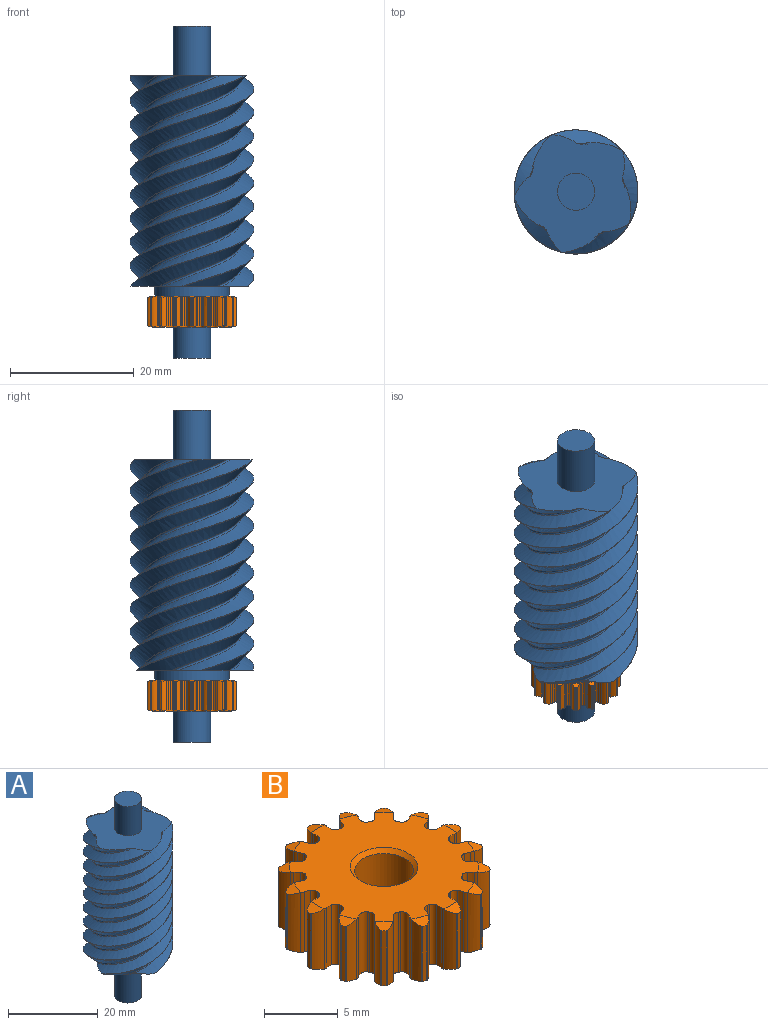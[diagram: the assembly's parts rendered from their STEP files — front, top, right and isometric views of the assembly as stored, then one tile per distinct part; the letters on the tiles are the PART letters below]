
ASSEMBLY  parts=2 mates=1
PART A: 33 faces, bbox 20.2x21.3x53.8 mm
  f0: cylinder r=10mm len=34mm, axis (0,0,-1), area -36.6mm2, adj f17,f22,f23,f26
  f1: bspline ~37.33x21.03mm, area 6.8mm2, adj f2,f17,f22,f26
  f2: bspline ~36.53x16.56mm, area 46.9mm2, adj f1,f3,f17,f22
  f3: bspline ~39.23x21.03mm, area 257mm2, adj f2,f4,f17,f22
  f4: cylinder r=10mm len=34mm, axis (0,0,-1), area -41.3mm2, adj f3,f17,f22,f27
  f5: bspline ~37.33x21.03mm, area 6.8mm2, adj f6,f17,f22,f27
  f6: bspline ~36.53x16.56mm, area 46.9mm2, adj f5,f7,f17,f22
  f7: bspline ~39.23x21.03mm, area 257mm2, adj f6,f8,f17,f22
  f8: cylinder r=10mm len=34mm, axis (0,0,-1), area -8.7mm2, adj f7,f17,f22,f28
  f9: bspline ~37.33x21.03mm, area 6.8mm2, adj f10,f17,f22,f28
  f10: bspline ~36.53x16.56mm, area 46.9mm2, adj f9,f11,f17,f22
  f11: bspline ~39.23x21.03mm, area 257mm2, adj f10,f12,f17,f22
  f12: cylinder r=10mm len=34mm, axis (0,0,-1), area -45.1mm2, adj f11,f17,f22,f29
  f13: bspline ~37.33x21.03mm, area 6.8mm2, adj f14,f17,f22,f29
  f14: bspline ~36.53x16.56mm, area 46.9mm2, adj f13,f15,f17,f22
  f15: bspline ~39.23x21.03mm, area 257mm2, adj f14,f16,f17,f22
  f16: cylinder r=10mm len=34mm, axis (0,0,-1), area -49.3mm2, adj f15,f17,f22,f30
  f17: plane 19.25x19.13mm, normal (0,0,1), area 217.7mm2, adj f0,f1,f2,f3,f4,f5,f6,f7
  f18: plane 6x6mm, normal (0,0,-1), area 28.3mm2, adj f19
  f19: cylinder r=3mm len=10mm, axis (0,0,-1), area 188.5mm2, adj f18,f20
  f20: plane 12x12mm, normal (0,0,-1), area 84.8mm2, adj f19,f21
  f21: cylinder r=6mm len=12mm, axis (0,0,-1), area 60.3mm2, adj f20,f22
  f22: plane 19.23x19.06mm, normal (0,0,-1), area 132.9mm2, adj f0,f1,f2,f3,f4,f5,f6,f7
  f23: bspline ~39.23x21.03mm, area 257mm2, adj f0,f17,f22,f24
  f24: bspline ~36.53x16.56mm, area 46.9mm2, adj f17,f22,f23,f25
  f25: bspline ~37.33x21.03mm, area 6.8mm2, adj f17,f22,f24,f30
  f26: bspline ~37.5x19.99mm, area 300.7mm2, adj f0,f1,f17,f22
  f27: bspline ~37.5x19.99mm, area 300.7mm2, adj f4,f5,f17,f22
  f28: bspline ~37.5x20mm, area 300.7mm2, adj f8,f9,f17,f22
  f29: bspline ~37.5x19.97mm, area 300.7mm2, adj f12,f13,f17,f22
  f30: bspline ~37.5x20mm, area 300.7mm2, adj f16,f17,f22,f25
  f31: cylinder r=3mm len=8mm, axis (0,0,-1), area 150.8mm2, adj f17,f32
  f32: plane 6x6mm, normal (0,0,1), area 28.3mm2, adj f31
PART B: 229 faces, bbox 14.4x14.4x5 mm
  f0: plane 12.8x12.8mm, normal (0,0,-1), area 96.1mm2, adj f1,f2,f3,f4,f5,f6,f7,f8
  f1: cone r=9.2mm half-angle=75deg, axis (0,0,1), area 0.7mm2, adj f0,f17,f63,f64,f65,f208
  f2: cone r=9.2mm half-angle=75deg, axis (0,0,1), area 0.7mm2, adj f0,f60,f61,f62,f199,f200
  f3: cone r=9.2mm half-angle=75deg, axis (0,0,1), area 0.7mm2, adj f0,f57,f58,f59,f190,f191
  f4: cone r=9.2mm half-angle=75deg, axis (0,0,1), area 0.7mm2, adj f0,f54,f55,f56,f181,f182
  f5: cone r=9.2mm half-angle=75deg, axis (0,0,1), area 0.7mm2, adj f0,f51,f52,f53,f172,f173
  f6: cone r=9.2mm half-angle=75deg, axis (0,0,1), area 0.7mm2, adj f0,f48,f49,f50,f163,f164
  f7: cone r=9.2mm half-angle=75deg, axis (0,0,1), area 0.7mm2, adj f0,f45,f46,f47,f154,f155
  f8: cone r=9.2mm half-angle=75deg, axis (0,0,1), area 0.7mm2, adj f0,f42,f43,f44,f145,f146
  f9: cone r=9.2mm half-angle=75deg, axis (0,0,1), area 0.7mm2, adj f0,f39,f40,f41,f136,f137
  f10: cone r=9.2mm half-angle=75deg, axis (0,0,1), area 0.7mm2, adj f0,f36,f37,f38,f127,f128
  f11: cone r=9.2mm half-angle=75deg, axis (0,0,1), area 0.7mm2, adj f0,f33,f34,f35,f118,f119
  f12: cone r=9.2mm half-angle=75deg, axis (0,0,1), area 0.7mm2, adj f0,f30,f31,f32,f109,f110
  f13: cone r=9.2mm half-angle=75deg, axis (0,0,1), area 0.7mm2, adj f0,f27,f28,f29,f100,f101
  f14: cone r=9.2mm half-angle=75deg, axis (0,0,1), area 0.7mm2, adj f0,f24,f25,f26,f91,f92
  f15: cone r=9.2mm half-angle=75deg, axis (0,0,1), area 0.7mm2, adj f0,f21,f22,f23,f82,f83
  f16: cone r=9.2mm half-angle=75deg, axis (0,0,1), area 0.7mm2, adj f0,f18,f19,f20,f73,f74
  f17: cylinder r=0.08mm len=4.59mm, axis (0,0,-1), area 0.3mm2, adj f1,f64,f65,f225
  f18: cylinder r=0.08mm len=4.59mm, axis (0,0,-1), area 0.3mm2, adj f16,f19,f73,f210
  f19: cylinder r=7.2mm len=4.57mm, axis (0,0,-1), area 1.4mm2, adj f16,f18,f20,f210
  f20: cylinder r=0.08mm len=4.59mm, axis (0,0,-1), area 0.3mm2, adj f16,f19,f74,f210
  f21: cylinder r=0.08mm len=4.59mm, axis (0,0,-1), area 0.3mm2, adj f15,f22,f82,f211
  f22: cylinder r=7.2mm len=4.57mm, axis (0,0,-1), area 1.4mm2, adj f15,f21,f23,f211
  f23: cylinder r=0.08mm len=4.59mm, axis (0,0,-1), area 0.3mm2, adj f15,f22,f83,f211
  f24: cylinder r=0.08mm len=4.59mm, axis (0,0,-1), area 0.3mm2, adj f14,f25,f91,f212
  f25: cylinder r=7.2mm len=4.57mm, axis (0,0,-1), area 1.4mm2, adj f14,f24,f26,f212
  f26: cylinder r=0.08mm len=4.59mm, axis (0,0,-1), area 0.3mm2, adj f14,f25,f92,f212
  f27: cylinder r=0.08mm len=4.59mm, axis (0,0,-1), area 0.3mm2, adj f13,f28,f100,f213
  f28: cylinder r=7.2mm len=4.57mm, axis (0,0,-1), area 1.4mm2, adj f13,f27,f29,f213
  f29: cylinder r=0.08mm len=4.59mm, axis (0,0,-1), area 0.3mm2, adj f13,f28,f101,f213
  f30: cylinder r=0.08mm len=4.59mm, axis (0,0,-1), area 0.3mm2, adj f12,f31,f109,f214
  f31: cylinder r=7.2mm len=4.57mm, axis (0,0,-1), area 1.4mm2, adj f12,f30,f32,f214
  f32: cylinder r=0.08mm len=4.59mm, axis (0,0,-1), area 0.3mm2, adj f12,f31,f110,f214
  f33: cylinder r=0.08mm len=4.59mm, axis (0,0,-1), area 0.3mm2, adj f11,f34,f118,f215
  f34: cylinder r=7.2mm len=4.57mm, axis (0,0,-1), area 1.4mm2, adj f11,f33,f35,f215
  f35: cylinder r=0.08mm len=4.59mm, axis (0,0,-1), area 0.3mm2, adj f11,f34,f119,f215
  f36: cylinder r=0.08mm len=4.59mm, axis (0,0,-1), area 0.3mm2, adj f10,f37,f127,f216
  f37: cylinder r=7.2mm len=4.57mm, axis (0,0,-1), area 1.4mm2, adj f10,f36,f38,f216
  f38: cylinder r=0.08mm len=4.59mm, axis (0,0,-1), area 0.3mm2, adj f10,f37,f128,f216
  f39: cylinder r=0.08mm len=4.59mm, axis (0,0,-1), area 0.3mm2, adj f9,f40,f136,f217
  f40: cylinder r=7.2mm len=4.57mm, axis (0,0,-1), area 1.4mm2, adj f9,f39,f41,f217
  f41: cylinder r=0.08mm len=4.59mm, axis (0,0,-1), area 0.3mm2, adj f9,f40,f137,f217
  f42: cylinder r=0.08mm len=4.59mm, axis (0,0,-1), area 0.3mm2, adj f8,f43,f145,f218
  f43: cylinder r=7.2mm len=4.57mm, axis (0,0,-1), area 1.4mm2, adj f8,f42,f44,f218
  f44: cylinder r=0.08mm len=4.59mm, axis (0,0,-1), area 0.3mm2, adj f8,f43,f146,f218
  f45: cylinder r=0.08mm len=4.59mm, axis (0,0,-1), area 0.3mm2, adj f7,f46,f154,f219
  f46: cylinder r=7.2mm len=4.57mm, axis (0,0,-1), area 1.4mm2, adj f7,f45,f47,f219
  f47: cylinder r=0.08mm len=4.59mm, axis (0,0,-1), area 0.3mm2, adj f7,f46,f155,f219
  f48: cylinder r=0.08mm len=4.59mm, axis (0,0,-1), area 0.3mm2, adj f6,f49,f163,f220
  f49: cylinder r=7.2mm len=4.57mm, axis (0,0,-1), area 1.4mm2, adj f6,f48,f50,f220
  f50: cylinder r=0.08mm len=4.59mm, axis (0,0,-1), area 0.3mm2, adj f6,f49,f164,f220
  f51: cylinder r=0.08mm len=4.59mm, axis (0,0,-1), area 0.3mm2, adj f5,f52,f172,f221
  f52: cylinder r=7.2mm len=4.57mm, axis (0,0,-1), area 1.4mm2, adj f5,f51,f53,f221
  f53: cylinder r=0.08mm len=4.59mm, axis (0,0,-1), area 0.3mm2, adj f5,f52,f173,f221
  f54: cylinder r=0.08mm len=4.59mm, axis (0,0,-1), area 0.3mm2, adj f4,f55,f181,f222
  f55: cylinder r=7.2mm len=4.57mm, axis (0,0,-1), area 1.4mm2, adj f4,f54,f56,f222
  f56: cylinder r=0.08mm len=4.59mm, axis (0,0,-1), area 0.3mm2, adj f4,f55,f182,f222
  f57: cylinder r=0.08mm len=4.59mm, axis (0,0,-1), area 0.3mm2, adj f3,f58,f190,f223
  f58: cylinder r=7.2mm len=4.57mm, axis (0,0,-1), area 1.4mm2, adj f3,f57,f59,f223
  f59: cylinder r=0.08mm len=4.59mm, axis (0,0,-1), area 0.3mm2, adj f3,f58,f191,f223
  f60: cylinder r=0.08mm len=4.59mm, axis (0,0,-1), area 0.3mm2, adj f2,f61,f199,f224
  f61: cylinder r=7.2mm len=4.57mm, axis (0,0,-1), area 1.4mm2, adj f2,f60,f62,f224
  f62: cylinder r=0.08mm len=4.59mm, axis (0,0,-1), area 0.3mm2, adj f2,f61,f200,f224
  f63: cylinder r=0.08mm len=4.59mm, axis (0,0,-1), area 0.3mm2, adj f1,f64,f208,f225
  f64: cylinder r=7.2mm len=4.57mm, axis (0,0,-1), area 1.4mm2, adj f1,f17,f63,f225
  f65: cylinder r=2mm len=5mm, axis (0,0,-1), area 4.4mm2, adj f1,f17,f66,f225
  f66: cylinder r=0.65mm len=5mm, axis (0,0,-1), area 1.3mm2, adj f0,f65,f67,f209
  f67: cylinder r=1.6mm len=5mm, axis (0,0,-1), area 2.4mm2, adj f0,f66,f68,f209
  f68: cylinder r=0.4mm len=5mm, axis (0,0,-1), area 2.5mm2, adj f0,f67,f69,f209
  f69: cylinder r=5.4mm len=5mm, axis (0,0,-1), area 0.9mm2, adj f0,f68,f70,f209
  f70: cylinder r=0.4mm len=5mm, axis (0,0,-1), area 2.5mm2, adj f0,f69,f71,f209
  f71: cylinder r=1.6mm len=5mm, axis (0,0,-1), area 2.4mm2, adj f0,f70,f72,f209
  f72: cylinder r=0.65mm len=5mm, axis (0,0,-1), area 1.3mm2, adj f0,f71,f73,f209
  f73: cylinder r=2mm len=5mm, axis (0,0,-1), area 4.4mm2, adj f16,f18,f72,f210
  f74: cylinder r=2mm len=5mm, axis (0,0,-1), area 4.4mm2, adj f16,f20,f75,f210
  f75: cylinder r=0.65mm len=5mm, axis (0,0,-1), area 1.3mm2, adj f0,f74,f76,f209
  f76: cylinder r=1.6mm len=5mm, axis (0,0,-1), area 2.4mm2, adj f0,f75,f77,f209
  f77: cylinder r=0.4mm len=5mm, axis (0,0,-1), area 2.5mm2, adj f0,f76,f78,f209
  f78: cylinder r=5.4mm len=5mm, axis (0,0,-1), area 0.9mm2, adj f0,f77,f79,f209
  f79: cylinder r=0.4mm len=5mm, axis (0,0,-1), area 2.5mm2, adj f0,f78,f80,f209
  f80: cylinder r=1.6mm len=5mm, axis (0,0,-1), area 2.4mm2, adj f0,f79,f81,f209
  f81: cylinder r=0.65mm len=5mm, axis (0,0,-1), area 1.3mm2, adj f0,f80,f82,f209
  f82: cylinder r=2mm len=5mm, axis (0,0,-1), area 4.4mm2, adj f15,f21,f81,f211
  f83: cylinder r=2mm len=5mm, axis (0,0,-1), area 4.4mm2, adj f15,f23,f84,f211
  f84: cylinder r=0.65mm len=5mm, axis (0,0,-1), area 1.3mm2, adj f0,f83,f85,f209
  f85: cylinder r=1.6mm len=5mm, axis (0,0,-1), area 2.4mm2, adj f0,f84,f86,f209
  f86: cylinder r=0.4mm len=5mm, axis (0,0,-1), area 2.5mm2, adj f0,f85,f87,f209
  f87: cylinder r=5.4mm len=5mm, axis (0,0,-1), area 0.9mm2, adj f0,f86,f88,f209
  f88: cylinder r=0.4mm len=5mm, axis (0,0,-1), area 2.5mm2, adj f0,f87,f89,f209
  f89: cylinder r=1.6mm len=5mm, axis (0,0,-1), area 2.4mm2, adj f0,f88,f90,f209
  f90: cylinder r=0.65mm len=5mm, axis (0,0,-1), area 1.3mm2, adj f0,f89,f91,f209
  f91: cylinder r=2mm len=5mm, axis (0,0,-1), area 4.4mm2, adj f14,f24,f90,f212
  f92: cylinder r=2mm len=5mm, axis (0,0,-1), area 4.4mm2, adj f14,f26,f93,f212
  f93: cylinder r=0.65mm len=5mm, axis (0,0,-1), area 1.3mm2, adj f0,f92,f94,f209
  f94: cylinder r=1.6mm len=5mm, axis (0,0,-1), area 2.4mm2, adj f0,f93,f95,f209
  f95: cylinder r=0.4mm len=5mm, axis (0,0,-1), area 2.5mm2, adj f0,f94,f96,f209
  f96: cylinder r=5.4mm len=5mm, axis (0,0,-1), area 0.9mm2, adj f0,f95,f97,f209
  f97: cylinder r=0.4mm len=5mm, axis (0,0,-1), area 2.5mm2, adj f0,f96,f98,f209
  f98: cylinder r=1.6mm len=5mm, axis (0,0,-1), area 2.4mm2, adj f0,f97,f99,f209
  f99: cylinder r=0.65mm len=5mm, axis (0,0,-1), area 1.3mm2, adj f0,f98,f100,f209
  f100: cylinder r=2mm len=5mm, axis (0,0,-1), area 4.4mm2, adj f13,f27,f99,f213
  f101: cylinder r=2mm len=5mm, axis (0,0,-1), area 4.4mm2, adj f13,f29,f102,f213
  f102: cylinder r=0.65mm len=5mm, axis (0,0,-1), area 1.3mm2, adj f0,f101,f103,f209
  f103: cylinder r=1.6mm len=5mm, axis (0,0,-1), area 2.4mm2, adj f0,f102,f104,f209
  f104: cylinder r=0.4mm len=5mm, axis (0,0,-1), area 2.5mm2, adj f0,f103,f105,f209
  f105: cylinder r=5.4mm len=5mm, axis (0,0,-1), area 0.9mm2, adj f0,f104,f106,f209
  f106: cylinder r=0.4mm len=5mm, axis (0,0,-1), area 2.5mm2, adj f0,f105,f107,f209
  f107: cylinder r=1.6mm len=5mm, axis (0,0,-1), area 2.4mm2, adj f0,f106,f108,f209
  f108: cylinder r=0.65mm len=5mm, axis (0,0,-1), area 1.3mm2, adj f0,f107,f109,f209
  f109: cylinder r=2mm len=5mm, axis (0,0,-1), area 4.4mm2, adj f12,f30,f108,f214
  f110: cylinder r=2mm len=5mm, axis (0,0,-1), area 4.4mm2, adj f12,f32,f111,f214
  f111: cylinder r=0.65mm len=5mm, axis (0,0,-1), area 1.3mm2, adj f0,f110,f112,f209
  f112: cylinder r=1.6mm len=5mm, axis (0,0,-1), area 2.4mm2, adj f0,f111,f113,f209
  f113: cylinder r=0.4mm len=5mm, axis (0,0,-1), area 2.5mm2, adj f0,f112,f114,f209
  f114: cylinder r=5.4mm len=5mm, axis (0,0,-1), area 0.9mm2, adj f0,f113,f115,f209
  f115: cylinder r=0.4mm len=5mm, axis (0,0,-1), area 2.5mm2, adj f0,f114,f116,f209
  f116: cylinder r=1.6mm len=5mm, axis (0,0,-1), area 2.4mm2, adj f0,f115,f117,f209
  f117: cylinder r=0.65mm len=5mm, axis (0,0,-1), area 1.3mm2, adj f0,f116,f118,f209
  f118: cylinder r=2mm len=5mm, axis (0,0,-1), area 4.4mm2, adj f11,f33,f117,f215
  f119: cylinder r=2mm len=5mm, axis (0,0,-1), area 4.4mm2, adj f11,f35,f120,f215
  f120: cylinder r=0.65mm len=5mm, axis (0,0,-1), area 1.3mm2, adj f0,f119,f121,f209
  f121: cylinder r=1.6mm len=5mm, axis (0,0,-1), area 2.4mm2, adj f0,f120,f122,f209
  f122: cylinder r=0.4mm len=5mm, axis (0,0,-1), area 2.5mm2, adj f0,f121,f123,f209
  f123: cylinder r=5.4mm len=5mm, axis (0,0,-1), area 0.9mm2, adj f0,f122,f124,f209
  f124: cylinder r=0.4mm len=5mm, axis (0,0,-1), area 2.5mm2, adj f0,f123,f125,f209
  f125: cylinder r=1.6mm len=5mm, axis (0,0,-1), area 2.4mm2, adj f0,f124,f126,f209
  f126: cylinder r=0.65mm len=5mm, axis (0,0,-1), area 1.3mm2, adj f0,f125,f127,f209
  f127: cylinder r=2mm len=5mm, axis (0,0,-1), area 4.4mm2, adj f10,f36,f126,f216
  f128: cylinder r=2mm len=5mm, axis (0,0,-1), area 4.4mm2, adj f10,f38,f129,f216
  f129: cylinder r=0.65mm len=5mm, axis (0,0,-1), area 1.3mm2, adj f0,f128,f130,f209
  f130: cylinder r=1.6mm len=5mm, axis (0,0,-1), area 2.4mm2, adj f0,f129,f131,f209
  f131: cylinder r=0.4mm len=5mm, axis (0,0,-1), area 2.5mm2, adj f0,f130,f132,f209
  f132: cylinder r=5.4mm len=5mm, axis (0,0,-1), area 0.9mm2, adj f0,f131,f133,f209
  f133: cylinder r=0.4mm len=5mm, axis (0,0,-1), area 2.5mm2, adj f0,f132,f134,f209
  f134: cylinder r=1.6mm len=5mm, axis (0,0,-1), area 2.4mm2, adj f0,f133,f135,f209
  f135: cylinder r=0.65mm len=5mm, axis (0,0,-1), area 1.3mm2, adj f0,f134,f136,f209
  f136: cylinder r=2mm len=5mm, axis (0,0,-1), area 4.4mm2, adj f9,f39,f135,f217
  f137: cylinder r=2mm len=5mm, axis (0,0,-1), area 4.4mm2, adj f9,f41,f138,f217
  f138: cylinder r=0.65mm len=5mm, axis (0,0,-1), area 1.3mm2, adj f0,f137,f139,f209
  f139: cylinder r=1.6mm len=5mm, axis (0,0,-1), area 2.4mm2, adj f0,f138,f140,f209
  f140: cylinder r=0.4mm len=5mm, axis (0,0,-1), area 2.5mm2, adj f0,f139,f141,f209
  f141: cylinder r=5.4mm len=5mm, axis (0,0,-1), area 0.9mm2, adj f0,f140,f142,f209
  f142: cylinder r=0.4mm len=5mm, axis (0,0,-1), area 2.5mm2, adj f0,f141,f143,f209
  f143: cylinder r=1.6mm len=5mm, axis (0,0,-1), area 2.4mm2, adj f0,f142,f144,f209
  f144: cylinder r=0.65mm len=5mm, axis (0,0,-1), area 1.3mm2, adj f0,f143,f145,f209
  f145: cylinder r=2mm len=5mm, axis (0,0,-1), area 4.4mm2, adj f8,f42,f144,f218
  f146: cylinder r=2mm len=5mm, axis (0,0,-1), area 4.4mm2, adj f8,f44,f147,f218
  f147: cylinder r=0.65mm len=5mm, axis (0,0,-1), area 1.3mm2, adj f0,f146,f148,f209
  f148: cylinder r=1.6mm len=5mm, axis (0,0,-1), area 2.4mm2, adj f0,f147,f149,f209
  f149: cylinder r=0.4mm len=5mm, axis (0,0,-1), area 2.5mm2, adj f0,f148,f150,f209
  f150: cylinder r=5.4mm len=5mm, axis (0,0,-1), area 0.9mm2, adj f0,f149,f151,f209
  f151: cylinder r=0.4mm len=5mm, axis (0,0,-1), area 2.5mm2, adj f0,f150,f152,f209
  f152: cylinder r=1.6mm len=5mm, axis (0,0,-1), area 2.4mm2, adj f0,f151,f153,f209
  f153: cylinder r=0.65mm len=5mm, axis (0,0,-1), area 1.3mm2, adj f0,f152,f154,f209
  f154: cylinder r=2mm len=5mm, axis (0,0,-1), area 4.4mm2, adj f7,f45,f153,f219
  f155: cylinder r=2mm len=5mm, axis (0,0,-1), area 4.4mm2, adj f7,f47,f156,f219
  f156: cylinder r=0.65mm len=5mm, axis (0,0,-1), area 1.3mm2, adj f0,f155,f157,f209
  f157: cylinder r=1.6mm len=5mm, axis (0,0,-1), area 2.4mm2, adj f0,f156,f158,f209
  f158: cylinder r=0.4mm len=5mm, axis (0,0,-1), area 2.5mm2, adj f0,f157,f159,f209
  f159: cylinder r=5.4mm len=5mm, axis (0,0,-1), area 0.9mm2, adj f0,f158,f160,f209
  f160: cylinder r=0.4mm len=5mm, axis (0,0,-1), area 2.5mm2, adj f0,f159,f161,f209
  f161: cylinder r=1.6mm len=5mm, axis (0,0,-1), area 2.4mm2, adj f0,f160,f162,f209
  f162: cylinder r=0.65mm len=5mm, axis (0,0,-1), area 1.3mm2, adj f0,f161,f163,f209
  f163: cylinder r=2mm len=5mm, axis (0,0,-1), area 4.4mm2, adj f6,f48,f162,f220
  f164: cylinder r=2mm len=5mm, axis (0,0,-1), area 4.4mm2, adj f6,f50,f165,f220
  f165: cylinder r=0.65mm len=5mm, axis (0,0,-1), area 1.3mm2, adj f0,f164,f166,f209
  f166: cylinder r=1.6mm len=5mm, axis (0,0,-1), area 2.4mm2, adj f0,f165,f167,f209
  f167: cylinder r=0.4mm len=5mm, axis (0,0,-1), area 2.5mm2, adj f0,f166,f168,f209
  f168: cylinder r=5.4mm len=5mm, axis (0,0,-1), area 0.9mm2, adj f0,f167,f169,f209
  f169: cylinder r=0.4mm len=5mm, axis (0,0,-1), area 2.5mm2, adj f0,f168,f170,f209
  f170: cylinder r=1.6mm len=5mm, axis (0,0,-1), area 2.4mm2, adj f0,f169,f171,f209
  f171: cylinder r=0.65mm len=5mm, axis (0,0,-1), area 1.3mm2, adj f0,f170,f172,f209
  f172: cylinder r=2mm len=5mm, axis (0,0,-1), area 4.4mm2, adj f5,f51,f171,f221
  f173: cylinder r=2mm len=5mm, axis (0,0,-1), area 4.4mm2, adj f5,f53,f174,f221
  f174: cylinder r=0.65mm len=5mm, axis (0,0,-1), area 1.3mm2, adj f0,f173,f175,f209
  f175: cylinder r=1.6mm len=5mm, axis (0,0,-1), area 2.4mm2, adj f0,f174,f176,f209
  f176: cylinder r=0.4mm len=5mm, axis (0,0,-1), area 2.5mm2, adj f0,f175,f177,f209
  f177: cylinder r=5.4mm len=5mm, axis (0,0,-1), area 0.9mm2, adj f0,f176,f178,f209
  f178: cylinder r=0.4mm len=5mm, axis (0,0,-1), area 2.5mm2, adj f0,f177,f179,f209
  f179: cylinder r=1.6mm len=5mm, axis (0,0,-1), area 2.4mm2, adj f0,f178,f180,f209
  f180: cylinder r=0.65mm len=5mm, axis (0,0,-1), area 1.3mm2, adj f0,f179,f181,f209
  f181: cylinder r=2mm len=5mm, axis (0,0,-1), area 4.4mm2, adj f4,f54,f180,f222
  f182: cylinder r=2mm len=5mm, axis (0,0,-1), area 4.4mm2, adj f4,f56,f183,f222
  f183: cylinder r=0.65mm len=5mm, axis (0,0,-1), area 1.3mm2, adj f0,f182,f184,f209
  f184: cylinder r=1.6mm len=5mm, axis (0,0,-1), area 2.4mm2, adj f0,f183,f185,f209
  f185: cylinder r=0.4mm len=5mm, axis (0,0,-1), area 2.5mm2, adj f0,f184,f186,f209
  f186: cylinder r=5.4mm len=5mm, axis (0,0,-1), area 0.9mm2, adj f0,f185,f187,f209
  f187: cylinder r=0.4mm len=5mm, axis (0,0,-1), area 2.5mm2, adj f0,f186,f188,f209
  f188: cylinder r=1.6mm len=5mm, axis (0,0,-1), area 2.4mm2, adj f0,f187,f189,f209
  f189: cylinder r=0.65mm len=5mm, axis (0,0,-1), area 1.3mm2, adj f0,f188,f190,f209
  f190: cylinder r=2mm len=5mm, axis (0,0,-1), area 4.4mm2, adj f3,f57,f189,f223
  f191: cylinder r=2mm len=5mm, axis (0,0,-1), area 4.4mm2, adj f3,f59,f192,f223
  f192: cylinder r=0.65mm len=5mm, axis (0,0,-1), area 1.3mm2, adj f0,f191,f193,f209
  f193: cylinder r=1.6mm len=5mm, axis (0,0,-1), area 2.4mm2, adj f0,f192,f194,f209
  f194: cylinder r=0.4mm len=5mm, axis (0,0,-1), area 2.5mm2, adj f0,f193,f195,f209
  f195: cylinder r=5.4mm len=5mm, axis (0,0,-1), area 0.9mm2, adj f0,f194,f196,f209
  f196: cylinder r=0.4mm len=5mm, axis (0,0,-1), area 2.5mm2, adj f0,f195,f197,f209
  f197: cylinder r=1.6mm len=5mm, axis (0,0,-1), area 2.4mm2, adj f0,f196,f198,f209
  f198: cylinder r=0.65mm len=5mm, axis (0,0,-1), area 1.3mm2, adj f0,f197,f199,f209
  f199: cylinder r=2mm len=5mm, axis (0,0,-1), area 4.4mm2, adj f2,f60,f198,f224
  f200: cylinder r=2mm len=5mm, axis (0,0,-1), area 4.4mm2, adj f2,f62,f201,f224
  f201: cylinder r=0.65mm len=5mm, axis (0,0,-1), area 1.3mm2, adj f0,f200,f202,f209
  f202: cylinder r=1.6mm len=5mm, axis (0,0,-1), area 2.4mm2, adj f0,f201,f203,f209
  f203: cylinder r=0.4mm len=5mm, axis (0,0,-1), area 2.5mm2, adj f0,f202,f204,f209
  f204: cylinder r=5.4mm len=5mm, axis (0,0,-1), area 0.9mm2, adj f0,f203,f205,f209
  f205: cylinder r=0.4mm len=5mm, axis (0,0,-1), area 2.5mm2, adj f0,f204,f206,f209
  f206: cylinder r=1.6mm len=5mm, axis (0,0,-1), area 2.4mm2, adj f0,f205,f207,f209
  f207: cylinder r=0.65mm len=5mm, axis (0,0,-1), area 1.3mm2, adj f0,f206,f208,f209
  f208: cylinder r=2mm len=5mm, axis (0,0,-1), area 4.4mm2, adj f1,f63,f207,f225
  f209: plane 12.8x12.8mm, normal (0,0,1), area 96.1mm2, adj f66,f67,f68,f69,f70,f71,f72,f75
  f210: cone r=6.4mm half-angle=75deg, axis (0,0,-1), area 0.7mm2, adj f18,f19,f20,f73,f74,f209
  f211: cone r=6.4mm half-angle=75deg, axis (0,0,-1), area 0.7mm2, adj f21,f22,f23,f82,f83,f209
  f212: cone r=6.4mm half-angle=75deg, axis (0,0,-1), area 0.7mm2, adj f24,f25,f26,f91,f92,f209
  f213: cone r=6.4mm half-angle=75deg, axis (0,0,-1), area 0.7mm2, adj f27,f28,f29,f100,f101,f209
  f214: cone r=6.4mm half-angle=75deg, axis (0,0,-1), area 0.7mm2, adj f30,f31,f32,f109,f110,f209
  f215: cone r=6.4mm half-angle=75deg, axis (0,0,-1), area 0.7mm2, adj f33,f34,f35,f118,f119,f209
  f216: cone r=6.4mm half-angle=75deg, axis (0,0,-1), area 0.7mm2, adj f36,f37,f38,f127,f128,f209
  f217: cone r=6.4mm half-angle=75deg, axis (0,0,-1), area 0.7mm2, adj f39,f40,f41,f136,f137,f209
  f218: cone r=6.4mm half-angle=75deg, axis (0,0,-1), area 0.7mm2, adj f42,f43,f44,f145,f146,f209
  f219: cone r=6.4mm half-angle=75deg, axis (0,0,-1), area 0.7mm2, adj f45,f46,f47,f154,f155,f209
  f220: cone r=6.4mm half-angle=75deg, axis (0,0,-1), area 0.7mm2, adj f48,f49,f50,f163,f164,f209
  f221: cone r=6.4mm half-angle=75deg, axis (0,0,-1), area 0.7mm2, adj f51,f52,f53,f172,f173,f209
  f222: cone r=6.4mm half-angle=75deg, axis (0,0,-1), area 0.7mm2, adj f54,f55,f56,f181,f182,f209
  f223: cone r=6.4mm half-angle=75deg, axis (0,0,-1), area 0.7mm2, adj f57,f58,f59,f190,f191,f209
  f224: cone r=6.4mm half-angle=75deg, axis (0,0,-1), area 0.7mm2, adj f60,f61,f62,f199,f200,f209
  f225: cone r=6.4mm half-angle=75deg, axis (0,0,-1), area 0.7mm2, adj f17,f63,f64,f65,f208,f209
  f226: cylinder r=2mm len=4.4mm, axis (0,0,-1), area 55.3mm2, adj f227,f228
  f227: cone r=2.3mm half-angle=45deg, axis (0,0,-1), area 5.7mm2, adj f0,f226
  f228: cone r=2mm half-angle=45deg, axis (0,0,1), area 5.7mm2, adj f209,f226
PLACE A t=(0.57,0.68,-4.66)mm
PLACE B t=(0.57,0.68,-27.46)mm
MATE fastened B.f1 <-> A.f0  axis (0,0,1) through (0.57,0.68,-22.46)mm
